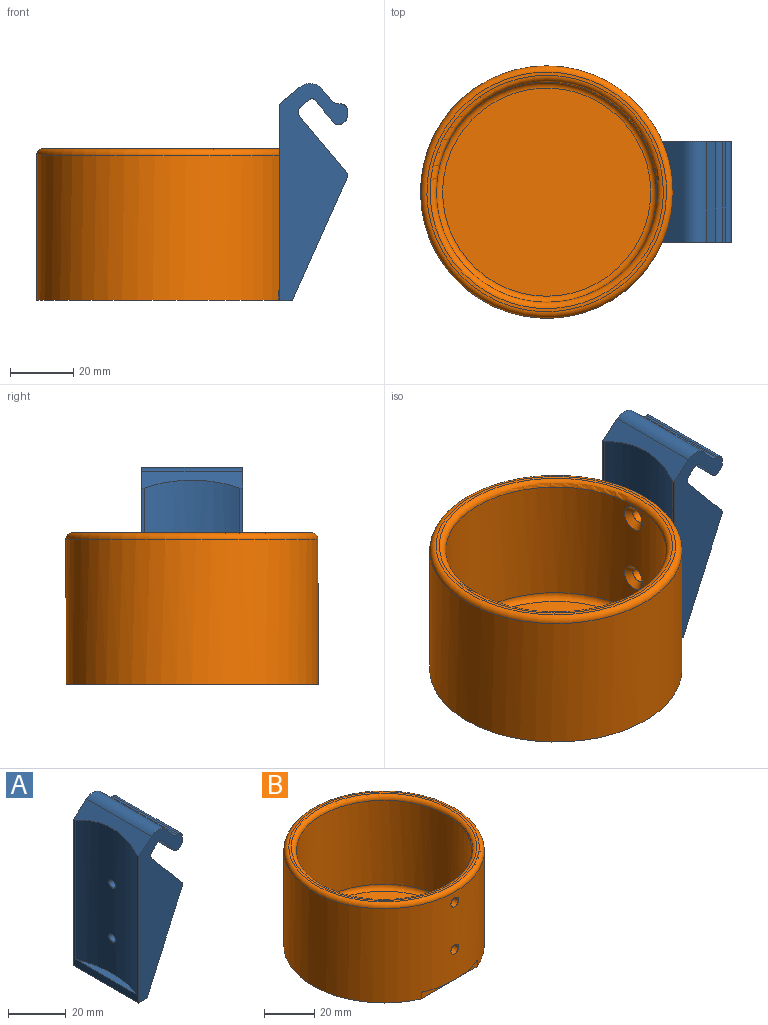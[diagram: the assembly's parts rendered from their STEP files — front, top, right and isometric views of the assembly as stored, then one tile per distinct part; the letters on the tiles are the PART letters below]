
ASSEMBLY  parts=2 mates=1
PART A: 27 faces, bbox 21.5x32x68.8 mm
  f0: plane 62.29x32mm, normal (-1,0,0), area 194.1mm2, adj f7,f8,f11,f12,f20,f21
  f1: plane 32x3.06mm, normal (0.64,0,-0.77), area 128mm2, adj f11,f12,f18,f19
  f2: plane 32x7.28mm, normal (-0.77,0,-0.64), area 304mm2, adj f11,f12,f14,f19
  f3: plane 32x0.82mm, normal (0.64,0,-0.77), area 34.2mm2, adj f11,f12,f14,f15
  f4: plane 32x1.93mm, normal (1,0,0), area 61.6mm2, adj f11,f12,f15,f16
  f5: plane 32x0.68mm, normal (0,0,1), area 21.7mm2, adj f11,f12,f13,f16
  f6: plane 32x3.65mm, normal (0.77,0,0.64), area 152.3mm2, adj f11,f12,f13,f26
  f7: plane 32x6.41mm, normal (-0.64,0,0.77), area 187.9mm2, adj f0,f11,f12,f20,f26
  f8: plane 32x4mm, normal (0,0,-1), area 128mm2, adj f0,f9,f11,f12
  f9: plane 38.82x32mm, normal (0.91,0,-0.41), area 1360.3mm2, adj f8,f11,f12,f17
  f10: plane 32x17.53mm, normal (0.77,0,0.64), area 732.4mm2, adj f11,f12,f17,f18
  f11: plane 68.84x21.5mm, normal (0,-1,0), area 905.6mm2, adj f0,f1,f2,f3,f4,f5,f6,f7
  f12: plane 68.84x21.5mm, normal (0,1,0), area 905.6mm2, adj f0,f1,f2,f3,f4,f5,f6,f7
  f13: cylinder r=3mm len=32mm, axis (0,1,0), area 83.8mm2, adj f5,f6,f11,f12
  f14: cylinder r=2mm len=32mm, axis (0,1,0), area 100.5mm2, adj f2,f3,f11,f12
  f15: cylinder r=2mm len=32mm, axis (0,1,0), area 55.9mm2, adj f3,f4,f11,f12
  f16: cylinder r=2mm len=32mm, axis (0,1,0), area 100.5mm2, adj f4,f5,f11,f12
  f17: cylinder r=2mm len=32mm, axis (0,1,0), area 71.5mm2, adj f9,f10,f11,f12
  f18: cylinder r=2mm len=32mm, axis (0,1,0), area 100.5mm2, adj f1,f10,f11,f12
  f19: cylinder r=1mm len=32mm, axis (0,-1,0), area 50.3mm2, adj f1,f2,f11,f12
  f20: cylinder r=40mm len=61.72mm, axis (0,0,-1), area 1881.8mm2, adj f0,f7,f21,f23,f25
  f21: plane 30.4x3mm, normal (0,0,1), area 61.3mm2, adj f0,f20
  f22: plane 3.2x3.2mm, normal (-1,0,0), area 8mm2, adj f23
  f23: cylinder r=1.6mm len=7.03mm, axis (-1,0,0), area 70.5mm2, adj f20,f22
  f24: plane 3.2x3.2mm, normal (-1,0,0), area 8mm2, adj f25
  f25: cylinder r=1.6mm len=7.03mm, axis (-1,0,0), area 70.5mm2, adj f20,f24
  f26: cylinder r=5mm len=32mm, axis (0,1,0), area 251.3mm2, adj f6,f7,f11,f12
PART B: 14 faces, bbox 86.6x86.6x48 mm
  f0: plane 80x76.8mm, normal (0,0,-1), area 4959.1mm2, adj f2,f10
  f1: cylinder r=35mm len=70mm, axis (0,0,-1), area 8911.3mm2, adj f5,f6,f12,f13
  f2: cylinder r=40mm len=80mm, axis (0,0,-1), area 11430.7mm2, adj f0,f7,f8,f9,f10,f11
  f3: plane 76x76mm, normal (0,0,1), area 235.6mm2, adj f6,f7
  f4: plane 66x66mm, normal (0,0,1), area 3421.2mm2, adj f5
  f5: torus R=33mm, axis (0,0,-1), area 676.5mm2, adj f1,f4
  f6: torus R=37mm, axis (0,0,1), area 705.2mm2, adj f1,f3
  f7: torus R=38mm, axis (0,0,1), area 775.2mm2, adj f2,f3
  f8: cylinder r=2.2mm len=4.4mm, axis (0,-1,0), area 41.5mm2, adj f2,f12
  f9: cylinder r=2.2mm len=4.4mm, axis (0,-1,0), area 41.5mm2, adj f2,f13
  f10: plane 31.35x3.1mm, normal (0,-1,0), area 97.2mm2, adj f0,f2,f11
  f11: plane 31.35x3.2mm, normal (0,0,-1), area 67.4mm2, adj f2,f10
  f12: bspline ~8.4x7.95mm, area 54.3mm2, adj f1,f8
  f13: bspline ~8.4x7.95mm, area 54.3mm2, adj f1,f9
PLACE A t=(10.41,42.31,-14.35)mm
PLACE B rot(axis=(0,0,1),90deg) t=(-26.68,26.31,-14.35)mm
MATE pin_slot B.f9 <-> A.f25  axis (1,0,0) through (13.34,26.31,23.65)mm
